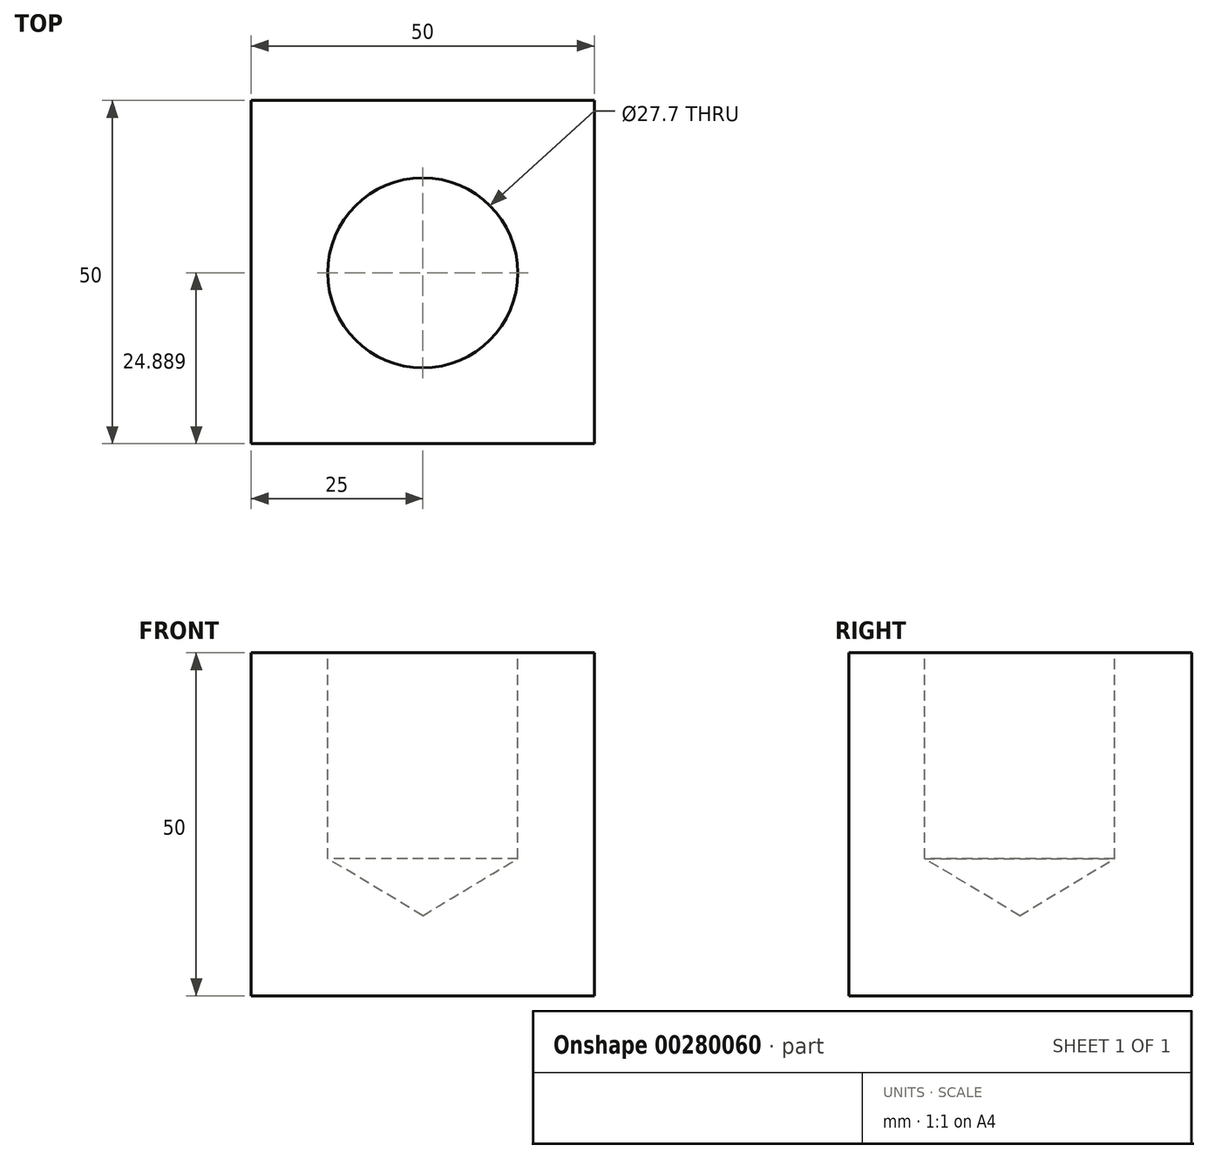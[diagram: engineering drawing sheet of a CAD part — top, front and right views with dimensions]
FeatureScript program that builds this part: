
annotation { "Feature Type Name" : "Feature", "Feature Type Description" : "" }
export const myFeature = defineFeature(function(context is Context, id is Id, definition is map)
    precondition{}
    {
        {
            var Q0;
            Q0=qCreatedBy(makeId("Front.planeOp"),FACE);
            var sketch = newSketch(context, id + "F0", { "sketchPlane" : qUnion([Q0])});
            skLineSegment(sketch, "E0.bottom", {"start": v(0, 0) * mm, "end": v(50, 0) * mm});
            skLineSegment(sketch, "E0.top", {"start": v(0, 50) * mm, "end": v(50, 50) * mm});
            skLineSegment(sketch, "E0.left", {"start": v(0, 0) * mm, "end": v(0, 50) * mm});
            skLineSegment(sketch, "E0.right", {"start": v(50, 0) * mm, "end": v(50, 50) * mm});
            skSolve(sketch);
        }
        {
            var Q0;
            Q0=makeQuery(id+"F0.imprint","IMPRINT",FACE,{"disambiguationData":[TD([[makeQuery(id+"F0.imprint","IMPRINT",EDGE,{"derivedFrom":sQuery(id+"F0.wireOp",EDGE,"E0.bottom")}),1.0]])]});
            var sketch = newSketch(context, id + "F1", { "sketchPlane" : qUnion([Q0])});
            skSolve(sketch);
        }
        {
            var Q0;
            Q0=makeQuery(id+"F1.imprint","IMPRINT",FACE,{"disambiguationData":[TD([[makeQuery(id+"F1.imprint","IMPRINT",EDGE,{"derivedFrom":makeQuery(id+"F0.imprint","IMPRINT",EDGE,{"derivedFrom":sQuery(id+"F0.wireOp",EDGE,"E0.bottom")})}),1.0]])]});
            extrude(context, id + "F2", {"entities" : qUnion([Q0]), "depth" : 50 * mm});
        }
        {
            var Q0;
            Q0=makeQuery(id+"F2.opExtrude","SWEPT_FACE",FACE,{"disambiguationData":[OSD([sQuery(id+"F0.wireOp",EDGE,"E0.top")])]});
            var sketch = newSketch(context, id + "F3", { "sketchPlane" : qUnion([Q0])});
            skCircle(sketch, "E1", {"center": v(25, -25.11) * mm, "radius": 11.73 * mm});
            skPoint(sketch, "E1.centerSnap0", {"position": v(25, -50) * mm});
            skSolve(sketch);
        }
        {
            var Q0;
            Q0=sQuery(id+"F3.wireOp",VERTEX,"E1.center");
            var Q1;
            Q1=makeQuery(id+"F2.opExtrude","SWEPT_BODY",BODY,{"disambiguationData":[OSD([sQuery(id+"F0.wireOp",EDGE,"E0.bottom"),sQuery(id+"F0.wireOp",EDGE,"E0.top"),sQuery(id+"F0.wireOp",EDGE,"E0.left"),sQuery(id+"F0.wireOp",EDGE,"E0.right")])]});
            hole(context, id + "F4", {"style" : HoleStyle.SIMPLE, "endStyle" : HoleEndStyle.BLIND, "holeDiameter" : 27.7 * mm, "holeDepth" : 30 * mm, "tappedDepth" : 12 * mm, "tapClearance" : 3, "locations" : qUnion([Q0]), "scope" : qUnion([Q1])});
        }
    });
